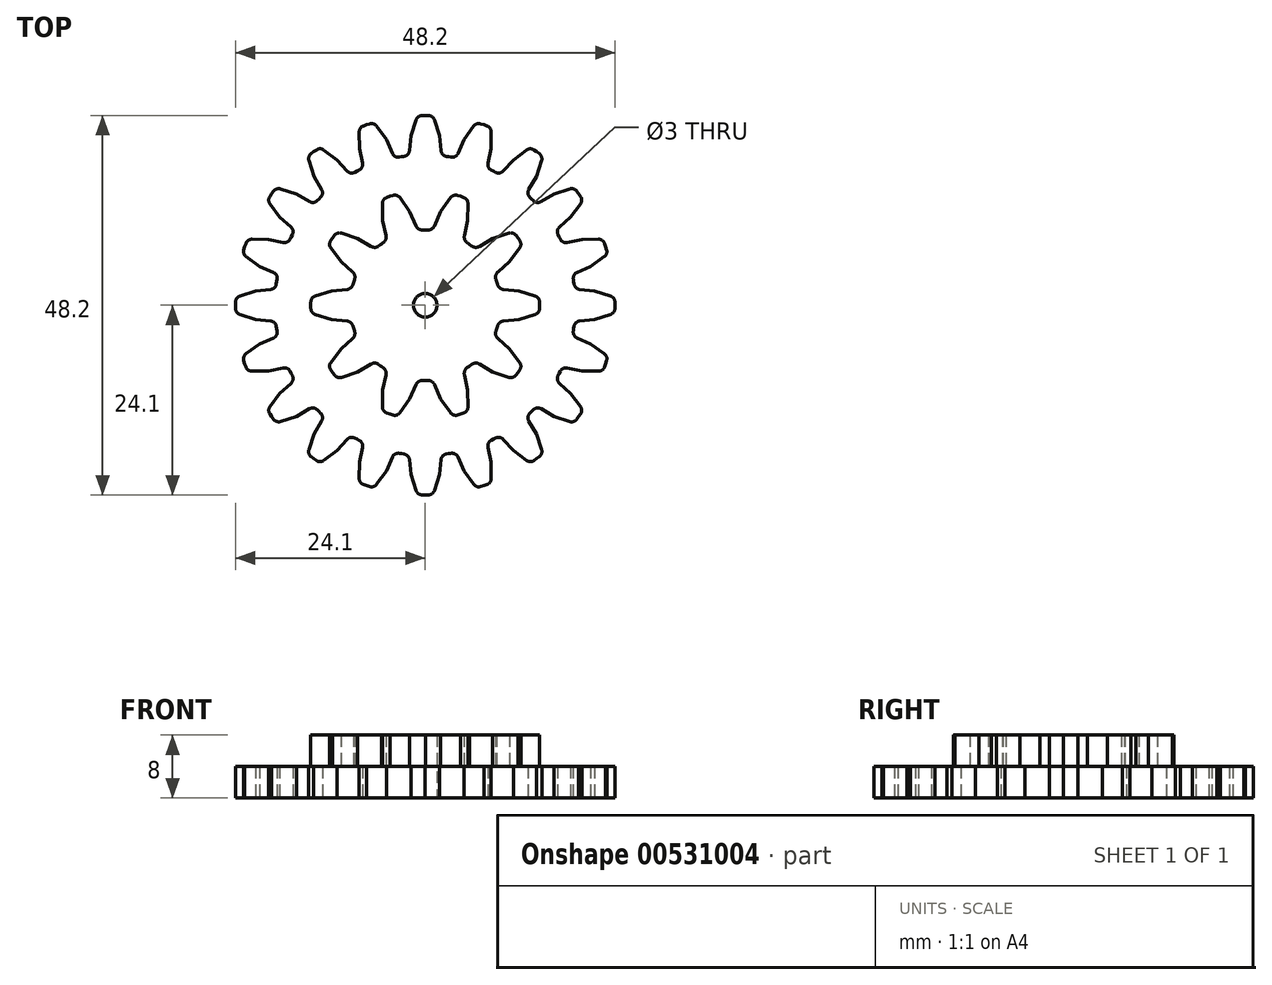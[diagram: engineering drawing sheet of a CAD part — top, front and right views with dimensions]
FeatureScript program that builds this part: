
annotation { "Feature Type Name" : "Feature", "Feature Type Description" : "" }
export const myFeature = defineFeature(function(context is Context, id is Id, definition is map)
    precondition{}
    {
        {
            assignVariable(context, id + "F0", {"name" : "debljina", "anyValue" : 4});
        }
        {
            assignVariable(context, id + "F1", {"name" : "nzuba", "anyValue" : 20});
        }
        {
            assignVariable(context, id + "F2", {"name" : "dupli", "anyValue" : 1});
        }
        {
            assignVariable(context, id + "F3", {"name" : "nzuba2", "anyValue" : getVariable(context, 'nzuba') / 2 * getVariable(context, 'dupli')});
        }
        {
            var Q0;
            Q0=qCreatedBy(makeId("Front.planeOp"),FACE);
            var sketch = newSketch(context, id + "F4", { "sketchPlane" : qUnion([Q0])});
            skLineSegment(sketch, "E0", {"start": v(0, 0) * mm, "end": v(0, 4) * mm, "construction": true});
            skSolve(sketch);
        }
        {
            var Q0;
            Q0=qCreatedBy(makeId("Top.planeOp"),FACE);
            var sketch = newSketch(context, id + "F5", { "sketchPlane" : qUnion([Q0])});
            skArc(sketch, "E1", {"start": v(18.86, 3) * mm, "mid": v(-19.1, 0) * mm, "end": v(18.86, -3) * mm});
            skCircle(sketch, "E2", {"center": v(0, 0) * mm, "radius": 24.1 * mm, "construction": true});
            skCircle(sketch, "E3", {"center": v(0, 0) * mm, "radius": 21.6 * mm, "construction": true});
            skLineSegment(sketch, "E4", {"start": v(0, 19.1) * mm, "end": v(0, 24.1) * mm, "construction": true});
            skLineSegment(sketch, "E5", {"start": v(-3.68, 23.82) * mm, "end": v(-3.3, 21.35) * mm, "construction": true});
            skLineSegment(sketch, "E6", {"start": v(-3.3, 21.35) * mm, "end": v(-2.92, 18.87) * mm, "construction": true});
            skLineSegment(sketch, "E7", {"start": v(0, 0) * mm, "end": v(24.1, 0) * mm, "construction": true});
            skLineSegment(sketch, "E8", {"start": v(0, 0) * mm, "end": v(18.86, 3) * mm});
            skLineSegment(sketch, "E9", {"start": v(0, 0) * mm, "end": v(19.62, 2) * mm, "construction": true});
            skPoint(sketch, "E10", {"position": v(19, 1.94) * mm});
            skLineSegment(sketch, "E11", {"start": v(19.62, 2) * mm, "end": v(21.52, 1.8) * mm});
            skLineSegment(sketch, "E12", {"start": v(21.52, 1.8) * mm, "end": v(23.53, 1.17) * mm});
            skLineSegment(sketch, "E13", {"start": v(24.09, 0.43) * mm, "end": v(24.1, 0) * mm});
            skPoint(sketch, "E14.visualSharp", {"position": v(24.08, 1) * mm});
            skArc(sketch, "E14.filletArc", {"start": v(24.09, 0.43) * mm, "mid": v(23.93, 0.89) * mm, "end": v(23.53, 1.17) * mm});
            skLineSegment(sketch, "E15.MirrorCS", {"start": v(19.62, -2) * mm, "end": v(21.52, -1.8) * mm});
            skLineSegment(sketch, "E16.MirrorCS", {"start": v(21.52, -1.8) * mm, "end": v(23.53, -1.17) * mm});
            skArc(sketch, "E17.MirrorCS", {"start": v(24.09, -0.43) * mm, "mid": v(23.93, -0.89) * mm, "end": v(23.53, -1.17) * mm});
            skLineSegment(sketch, "E18.MirrorCS", {"start": v(24.09, -0.43) * mm, "end": v(24.1, 0) * mm});
            skLineSegment(sketch, "E19.MirrorCS", {"start": v(0, 0) * mm, "end": v(18.86, -3) * mm});
            skCircle(sketch, "E20", {"center": v(0, 0) * mm, "radius": 1.5 * mm});
            skLineSegment(sketch, "E21", {"start": v(18.86, 3) * mm, "end": v(18.91, 2.67) * mm});
            skArc(sketch, "E22", {"start": v(18.91, 2.67) * mm, "mid": v(19.15, 2.22) * mm, "end": v(19.62, 2) * mm});
            skLineSegment(sketch, "E23.MirrorCS", {"start": v(18.86, -3) * mm, "end": v(18.91, -2.67) * mm});
            skArc(sketch, "E24.MirrorCS", {"start": v(18.91, -2.67) * mm, "mid": v(19.15, -2.22) * mm, "end": v(19.62, -2) * mm});
            skSolve(sketch);
        }
        {
            var Q0;
            Q0=makeQuery(id+"F5.imprint","IMPRINT",FACE,{"disambiguationData":[TD([[makeQuery(id+"F5.imprint","IMPRINT",EDGE,{"derivedFrom":sQuery(id+"F5.wireOp",EDGE,"E11")}),-1.0]])]});
            extrude(context, id + "F6", {"entities" : qUnion([Q0]), "depth" : 4 * mm, "offsetDistance" : 25 * mm});
        }
        {
            var Q0;
            Q0=makeQuery(id+"F6.opExtrude","SWEPT_BODY",BODY,{"disambiguationData":[OSD([sQuery(id+"F5.wireOp",EDGE,"E8"),sQuery(id+"F5.wireOp",EDGE,"Ccr5RPwP-yEiI-mMhH-aCbI-xiKkbVCYuAfT"),sQuery(id+"F5.wireOp",EDGE,"E11"),sQuery(id+"F5.wireOp",EDGE,"E12"),sQuery(id+"F5.wireOp",EDGE,"E13"),sQuery(id+"F5.wireOp",EDGE,"E14.filletArc"),sQuery(id+"F5.wireOp",EDGE,"434113d8-d490-4e0a-a8ba-07c452dbb1c90.MirrorCS"),sQuery(id+"F5.wireOp",EDGE,"E15.MirrorCS"),sQuery(id+"F5.wireOp",EDGE,"E16.MirrorCS"),sQuery(id+"F5.wireOp",EDGE,"E17.MirrorCS"),sQuery(id+"F5.wireOp",EDGE,"E18.MirrorCS"),sQuery(id+"F5.wireOp",EDGE,"E19.MirrorCS")])]});
            var Q1;
            Q1=sQuery(id+"F4.wireOp",EDGE,"E0");
            circularPattern(context, id + "F7", {"operationType" : NewBodyOperationType.ADD, "entities" : qUnion([Q0]), "axis" : qUnion([Q1]), "angle" : 360 * degree, "instanceCount" : getVariable(context, 'nzuba'), "equalSpace" : true, "computeTransformsWithoutBuiltin" : true});
        }
        {
            var Q0;
            {var subQ0=makeQuery(id+"F6.opExtrude","CAP_FACE",FACE,{"disambiguationData":[OSD([sQuery(id+"F5.wireOp",EDGE,"E8"),sQuery(id+"F5.wireOp",EDGE,"E11"),sQuery(id+"F5.wireOp",EDGE,"E12"),sQuery(id+"F5.wireOp",EDGE,"E13"),sQuery(id+"F5.wireOp",EDGE,"E14.filletArc"),sQuery(id+"F5.wireOp",EDGE,"E15.MirrorCS"),sQuery(id+"F5.wireOp",EDGE,"E16.MirrorCS"),sQuery(id+"F5.wireOp",EDGE,"E17.MirrorCS"),sQuery(id+"F5.wireOp",EDGE,"E18.MirrorCS"),sQuery(id+"F5.wireOp",EDGE,"E19.MirrorCS"),sQuery(id+"F5.wireOp",EDGE,"E20"),sQuery(id+"F5.wireOp",EDGE,"E21"),sQuery(id+"F5.wireOp",EDGE,"E22"),sQuery(id+"F5.wireOp",EDGE,"E23.MirrorCS"),sQuery(id+"F5.wireOp",EDGE,"E24.MirrorCS")])],"isStart":false});Q0=makeQuery(id+"F7.boolean.opBoolean","MERGE",FACE,{"derivedFrom":[subQ0,makeQuery(id+"F7.opPattern","COPY",FACE,{"derivedFrom":subQ0,"instanceName":"1"}),makeQuery(id+"F7.opPattern","COPY",FACE,{"derivedFrom":subQ0,"instanceName":"2"}),makeQuery(id+"F7.opPattern","COPY",FACE,{"derivedFrom":subQ0,"instanceName":"3"}),makeQuery(id+"F7.opPattern","COPY",FACE,{"derivedFrom":subQ0,"instanceName":"4"}),makeQuery(id+"F7.opPattern","COPY",FACE,{"derivedFrom":subQ0,"instanceName":"5"}),makeQuery(id+"F7.opPattern","COPY",FACE,{"derivedFrom":subQ0,"instanceName":"6"}),makeQuery(id+"F7.opPattern","COPY",FACE,{"derivedFrom":subQ0,"instanceName":"7"}),makeQuery(id+"F7.opPattern","COPY",FACE,{"derivedFrom":subQ0,"instanceName":"8"}),makeQuery(id+"F7.opPattern","COPY",FACE,{"derivedFrom":subQ0,"instanceName":"9"}),makeQuery(id+"F7.opPattern","COPY",FACE,{"derivedFrom":subQ0,"instanceName":"10"}),makeQuery(id+"F7.opPattern","COPY",FACE,{"derivedFrom":subQ0,"instanceName":"11"}),makeQuery(id+"F7.opPattern","COPY",FACE,{"derivedFrom":subQ0,"instanceName":"12"}),makeQuery(id+"F7.opPattern","COPY",FACE,{"derivedFrom":subQ0,"instanceName":"13"}),makeQuery(id+"F7.opPattern","COPY",FACE,{"derivedFrom":subQ0,"instanceName":"14"}),makeQuery(id+"F7.opPattern","COPY",FACE,{"derivedFrom":subQ0,"instanceName":"15"}),makeQuery(id+"F7.opPattern","COPY",FACE,{"derivedFrom":subQ0,"instanceName":"16"}),makeQuery(id+"F7.opPattern","COPY",FACE,{"derivedFrom":subQ0,"instanceName":"17"}),makeQuery(id+"F7.opPattern","COPY",FACE,{"derivedFrom":subQ0,"instanceName":"18"}),makeQuery(id+"F7.opPattern","COPY",FACE,{"derivedFrom":subQ0,"instanceName":"19"})]});}
            var sketch = newSketch(context, id + "F8", { "sketchPlane" : qUnion([Q0])});
            skArc(sketch, "E25", {"start": v(9.07, 3) * mm, "mid": v(-9.55, 0) * mm, "end": v(9.07, -3) * mm});
            skCircle(sketch, "E26", {"center": v(0, 0) * mm, "radius": 14.55 * mm, "construction": true});
            skCircle(sketch, "E27", {"center": v(0, 0) * mm, "radius": 12.05 * mm, "construction": true});
            skLineSegment(sketch, "E28", {"start": v(0, 9.55) * mm, "end": v(0, 14.55) * mm, "construction": true});
            skLineSegment(sketch, "E29", {"start": v(-2.22, 14.38) * mm, "end": v(-1.84, 11.9) * mm, "construction": true});
            skLineSegment(sketch, "E30", {"start": v(-1.84, 11.9) * mm, "end": v(-1.46, 9.44) * mm, "construction": true});
            skLineSegment(sketch, "E31", {"start": v(0, 0) * mm, "end": v(14.55, 0) * mm, "construction": true});
            skLineSegment(sketch, "E32", {"start": v(0, 0) * mm, "end": v(9.07, 3) * mm});
            skLineSegment(sketch, "E33", {"start": v(0, 0) * mm, "end": v(9.96, 2) * mm, "construction": true});
            skPoint(sketch, "E34", {"position": v(9.36, 1.88) * mm});
            skLineSegment(sketch, "E35", {"start": v(9.96, 2) * mm, "end": v(11.91, 1.8) * mm});
            skLineSegment(sketch, "E36", {"start": v(11.91, 1.8) * mm, "end": v(13.97, 1.17) * mm});
            skLineSegment(sketch, "E37", {"start": v(14.53, 0.43) * mm, "end": v(14.55, 0) * mm});
            skPoint(sketch, "E38.visualSharp", {"position": v(14.51, 1) * mm});
            skArc(sketch, "E38.filletArc", {"start": v(14.53, 0.43) * mm, "mid": v(14.37, 0.89) * mm, "end": v(13.97, 1.17) * mm});
            skLineSegment(sketch, "E39.MirrorCS", {"start": v(9.96, -2) * mm, "end": v(11.91, -1.8) * mm});
            skLineSegment(sketch, "E40.MirrorCS", {"start": v(11.91, -1.8) * mm, "end": v(13.97, -1.17) * mm});
            skArc(sketch, "E41.MirrorCS", {"start": v(14.53, -0.43) * mm, "mid": v(14.37, -0.89) * mm, "end": v(13.97, -1.17) * mm});
            skLineSegment(sketch, "E42.MirrorCS", {"start": v(14.53, -0.43) * mm, "end": v(14.55, 0) * mm});
            skLineSegment(sketch, "E43.MirrorCS", {"start": v(0, 0) * mm, "end": v(9.07, -3) * mm});
            skCircle(sketch, "E44", {"center": v(0, 0) * mm, "radius": 1.5 * mm});
            skLineSegment(sketch, "E45", {"start": v(9.07, 3) * mm, "end": v(9.2, 2.61) * mm});
            skArc(sketch, "E46", {"start": v(9.2, 2.61) * mm, "mid": v(9.48, 2.2) * mm, "end": v(9.96, 2) * mm});
            skLineSegment(sketch, "E47.MirrorCS", {"start": v(9.07, -3) * mm, "end": v(9.2, -2.61) * mm});
            skArc(sketch, "E48.MirrorCS", {"start": v(9.2, -2.61) * mm, "mid": v(9.48, -2.2) * mm, "end": v(9.96, -2) * mm});
            skSolve(sketch);
        }
        {
            var Q0;
            Q0=makeQuery(id+"F8.imprint","IMPRINT",FACE,{"disambiguationData":[TD([[makeQuery(id+"F8.imprint","IMPRINT",EDGE,{"derivedFrom":sQuery(id+"F8.wireOp",EDGE,"E35")}),-1.0]])]});
            extrude(context, id + "F9", {"entities" : qUnion([Q0]), "depth" : (getVariable(context, 'debljina') * getVariable(context, 'dupli')) * mm, "offsetDistance" : 25 * mm});
        }
        {
            var Q0;
            Q0=makeQuery(id+"F9.opExtrude","SWEPT_BODY",BODY,{"disambiguationData":[OSD([sQuery(id+"F8.wireOp",EDGE,"E32"),sQuery(id+"F8.wireOp",EDGE,"E35"),sQuery(id+"F8.wireOp",EDGE,"E36"),sQuery(id+"F8.wireOp",EDGE,"E37"),sQuery(id+"F8.wireOp",EDGE,"E38.filletArc"),sQuery(id+"F8.wireOp",EDGE,"E39.MirrorCS"),sQuery(id+"F8.wireOp",EDGE,"E40.MirrorCS"),sQuery(id+"F8.wireOp",EDGE,"E41.MirrorCS"),sQuery(id+"F8.wireOp",EDGE,"E42.MirrorCS"),sQuery(id+"F8.wireOp",EDGE,"E43.MirrorCS"),sQuery(id+"F8.wireOp",EDGE,"E44"),sQuery(id+"F8.wireOp",EDGE,"E45"),sQuery(id+"F8.wireOp",EDGE,"E46"),sQuery(id+"F8.wireOp",EDGE,"E47.MirrorCS"),sQuery(id+"F8.wireOp",EDGE,"E48.MirrorCS")])]});
            var Q1;
            Q1=sQuery(id+"F4.wireOp",EDGE,"E0");
            circularPattern(context, id + "F10", {"operationType" : NewBodyOperationType.ADD, "entities" : qUnion([Q0]), "axis" : qUnion([Q1]), "angle" : 360 * degree, "instanceCount" : getVariable(context, 'nzuba2'), "equalSpace" : true, "computeTransformsWithoutBuiltin" : true});
        }
    });
